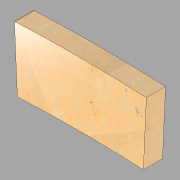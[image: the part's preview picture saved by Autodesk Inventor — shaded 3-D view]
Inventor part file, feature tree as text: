
AUTODESK INVENTOR PART (.ipt)
format: ipt  version: 2022.1 (Build 261234020, 234B)  size: 116,224 bytes
history: imported  units: in
note: dims shown in document units (in); Inventor stores cm internally (conversion verified against a paired STEP export)
features: imported_body x1
ambient origin geometry x8: Origin, YZ Plane, XZ Plane, XY Plane, X Axis, Y Axis, Z Axis, Center Point
bodies: Solid1 (imported_parasolid)
feature tree (1):
  imported_body  NMx_Import_Brep_tag  [imported B-rep: ~7 faces, bbox_mm=[1047.756234, 508.678939, 152.4]]
